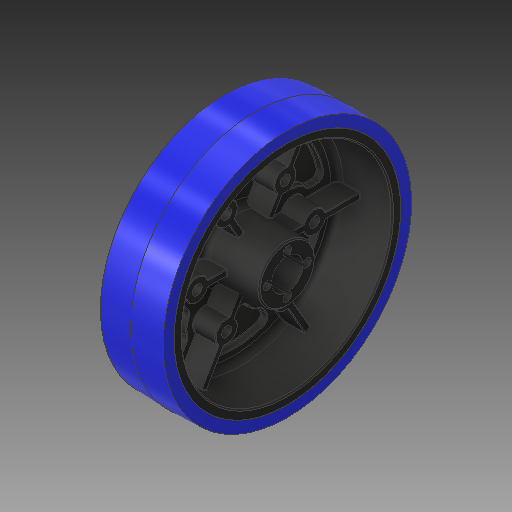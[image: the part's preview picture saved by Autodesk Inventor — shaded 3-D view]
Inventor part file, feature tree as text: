
AUTODESK INVENTOR PART (.ipt)
format: ipt  version: 2017 (Build 210142000, 142)  size: 2,230,272 bytes
history: native  units: in
note: dims shown in document units (in); Inventor stores cm internally (conversion verified against a paired STEP export)
features: other x4, sketch x1
ambient origin geometry x8: Origin, YZ Plane, XZ Plane, XY Plane, X Axis, Y Axis, Z Axis, Center Point
bodies: Solid1 (feature_tree), Solid2 (feature_tree)
feature tree (5):
  other  "am-2648_4inWheel8mmHubblu.ipt"
  other  "Solid1::am-2648_4inWheel8mmHubblu.ipt"
  other  "Solid2::am-2648_4inWheel8mmHubblu.ipt"
  other  "TaggingFeature1"
  sketch  "Sketch1"  dims[d0=0.3937in]
